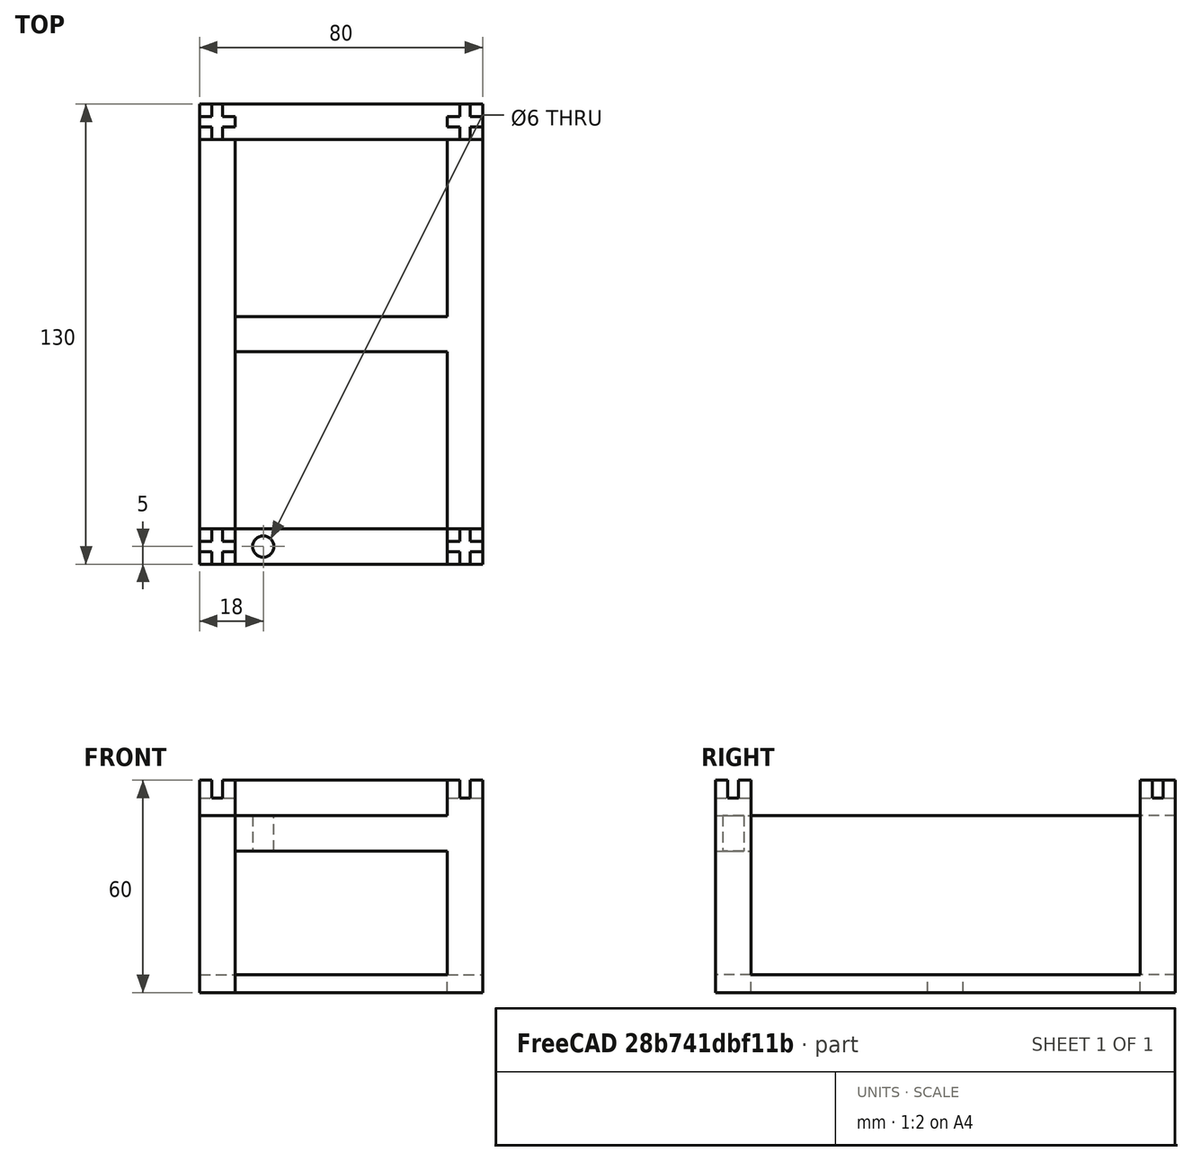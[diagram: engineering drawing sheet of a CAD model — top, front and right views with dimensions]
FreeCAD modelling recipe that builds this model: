
FCSTD DOCUMENT  (FreeCAD 0.21R0.20.1)
Label: SmallSampleMount01
License: All rights reserved
LicenseURL: https://en.wikipedia.org/wiki/All_rights_reserved
objects: Part::Box×18, Part::MultiFuse×7, Part::Cut×3, Part::Cylinder×1
note: 29 computed .brp shape members not serialized (recipe doc carries the construction recipe); baked Part::Feature solids carry a one-line shape summary decoded from their .brp

FEATURE [Part::Box] Box  label="Cube"
  AttacherType = Attacher::AttachEngine3D
  Height = 5
  Length = 80
  Width = 130
FEATURE [Part::Box] Box001  label="Cube001"
  AttacherType = Attacher::AttachEngine3D
  Height = 5
  Length = 60
  Placement = pos=(10,10,0) rot=(0,0,1;0rad)
  Width = 50
FEATURE [Part::Box] Box002  label="Cube002"
  AttacherType = Attacher::AttachEngine3D
  Height = 5
  Length = 60
  Placement = pos=(10,70,0) rot=(0,0,1;0rad)
  Width = 50
FEATURE [Part::MultiFuse] Fusion
  Shapes = -> [Box002,Box001]
FEATURE [Part::Cut] Cut
  Base = -> Box
  Tool = -> Fusion
FEATURE [Part::Box] Box003  label="Cube003"
  AttacherType = Attacher::AttachEngine3D
  Height = 60
  Length = 10
  Width = 10
FEATURE [Part::Box] Box004  label="Cube004"
  AttacherType = Attacher::AttachEngine3D
  Height = 60
  Length = 10
  Placement = pos=(0,120,0) rot=(0,0,1;0rad)
  Width = 10
FEATURE [Part::Box] Box005  label="Cube005"
  AttacherType = Attacher::AttachEngine3D
  Height = 60
  Length = 10
  Placement = pos=(70,120,0) rot=(0,0,1;0rad)
  Width = 10
FEATURE [Part::Box] Box006  label="Cube006"
  AttacherType = Attacher::AttachEngine3D
  Height = 60
  Length = 10
  Placement = pos=(70,0,0) rot=(0,0,1;0rad)
  Width = 10
FEATURE [Part::Box] Box007  label="Cube007"
  AttacherType = Attacher::AttachEngine3D
  Height = 10
  Length = 80
  Placement = pos=(0,0,50) rot=(0,0,1;0rad)
  Width = 10
FEATURE [Part::Box] Box008  label="Cube008"
  AttacherType = Attacher::AttachEngine3D
  Height = 10
  Length = 80
  Placement = pos=(0,120,50) rot=(0,0,1;0rad)
  Width = 10
FEATURE [Part::Cylinder] Cylinder
  Angle = 360
  AttacherType = Attacher::AttachEngine3D
  FirstAngle = 0
  Height = 10
  Placement = pos=(18,5,50) rot=(0,0,1;0rad)
  Radius = 3
  SecondAngle = 0
FEATURE [Part::Cut] Cut001
  Base = -> Box007
  Placement = pos=(0,0,-10) rot=(0,0,1;0rad)
  Tool = -> Cylinder
FEATURE [Part::Box] Box009  label="Cube009"
  AttacherType = Attacher::AttachEngine3D
  Height = 50
  Length = 10
  Width = 120
FEATURE [Part::Box] Box010  label="Cube010"
  AttacherType = Attacher::AttachEngine3D
  Height = 5
  Length = 3
  Placement = pos=(3.5,0,55) rot=(0,0,1;0rad)
  Width = 10
FEATURE [Part::Box] Box011  label="Cube011"
  AttacherType = Attacher::AttachEngine3D
  Height = 5
  Length = 10
  Placement = pos=(0,3.5,55) rot=(0,0,1;0rad)
  Width = 3
FEATURE [Part::MultiFuse] Fusion001
  Shapes = -> [Box011,Box010]
FEATURE [Part::Box] Box012  label="Cube012"
  AttacherType = Attacher::AttachEngine3D
  Height = 5
  Length = 3
  Placement = pos=(3.5,0,55) rot=(0,0,1;0rad)
  Width = 10
FEATURE [Part::Box] Box013  label="Cube013"
  AttacherType = Attacher::AttachEngine3D
  Height = 5
  Length = 10
  Placement = pos=(0,3.5,55) rot=(0,0,1;0rad)
  Width = 3
FEATURE [Part::MultiFuse] Fusion002
  Placement = pos=(0,120,0) rot=(0,0,1;0rad)
  Shapes = -> [Box013,Box012]
FEATURE [Part::Box] Box014  label="Cube014"
  AttacherType = Attacher::AttachEngine3D
  Height = 5
  Length = 3
  Placement = pos=(3.5,0,55) rot=(0,0,1;0rad)
  Width = 10
FEATURE [Part::Box] Box015  label="Cube015"
  AttacherType = Attacher::AttachEngine3D
  Height = 5
  Length = 10
  Placement = pos=(0,3.5,55) rot=(0,0,1;0rad)
  Width = 3
FEATURE [Part::Box] Box016  label="Cube016"
  AttacherType = Attacher::AttachEngine3D
  Height = 5
  Length = 3
  Placement = pos=(3.5,0,55) rot=(0,0,1;0rad)
  Width = 10
FEATURE [Part::Box] Box017  label="Cube017"
  AttacherType = Attacher::AttachEngine3D
  Height = 5
  Length = 10
  Placement = pos=(0,3.5,55) rot=(0,0,1;0rad)
  Width = 3
FEATURE [Part::MultiFuse] Fusion003
  Placement = pos=(70,0,0) rot=(0,0,1;0rad)
  Shapes = -> [Box015,Box014]
FEATURE [Part::MultiFuse] Fusion004
  Placement = pos=(70,120,0) rot=(0,0,1;0rad)
  Shapes = -> [Box017,Box016]
FEATURE [Part::MultiFuse] Fusion005
  Shapes = -> [Fusion004,Fusion001,Fusion002,Fusion003]
FEATURE [Part::MultiFuse] Fusion006
  Shapes = -> [Cut001,Box003,Box004,Box005,Box006,Box008,Cut]
FEATURE [Part::Cut] Cut002
  Base = -> Fusion006
  Tool = -> Fusion005
